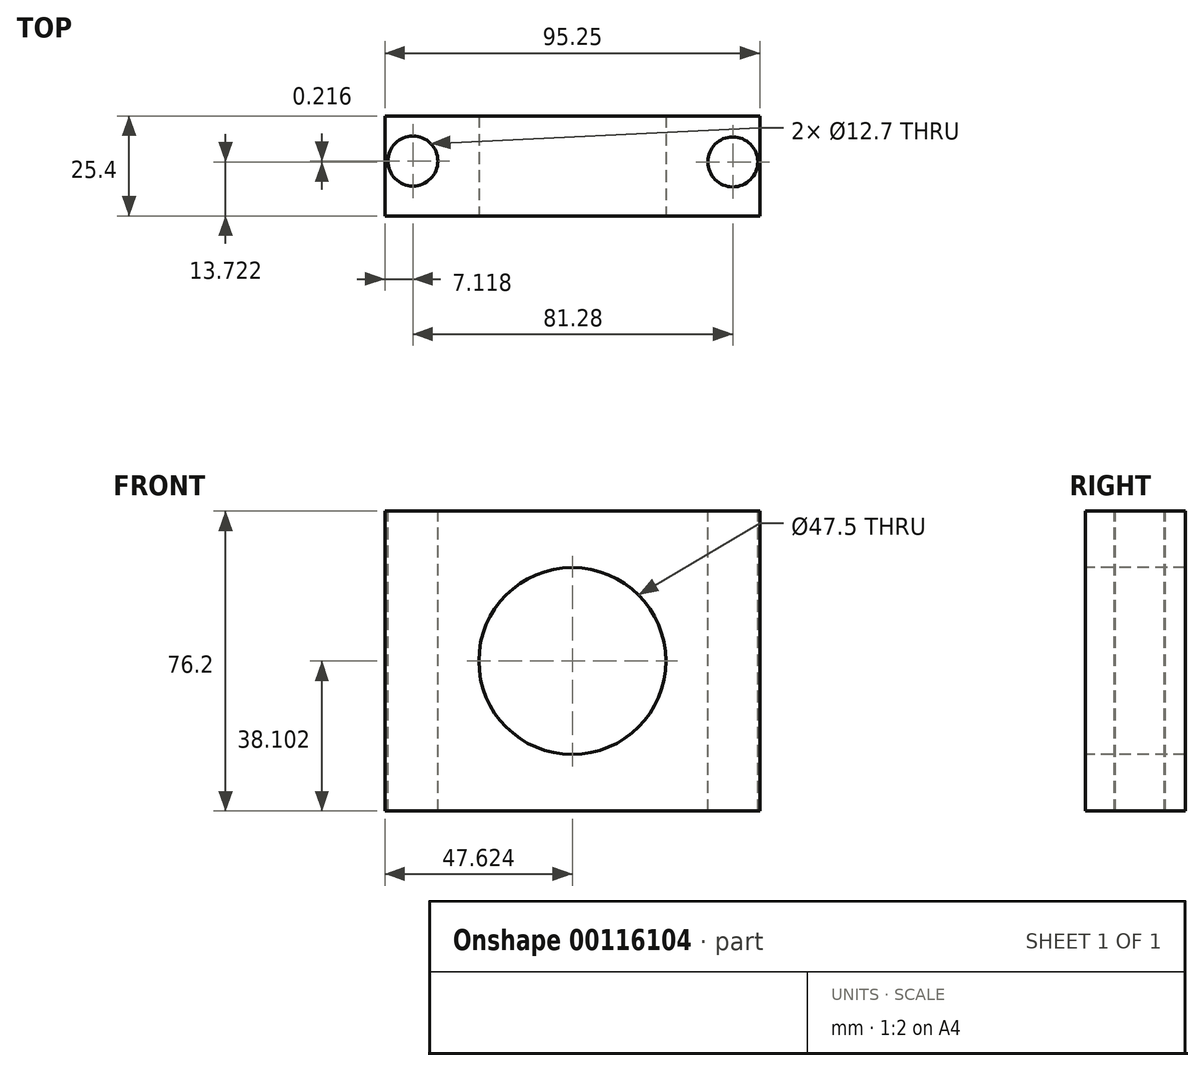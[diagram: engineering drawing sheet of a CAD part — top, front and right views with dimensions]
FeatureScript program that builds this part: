
annotation { "Feature Type Name" : "Feature", "Feature Type Description" : "" }
export const myFeature = defineFeature(function(context is Context, id is Id, definition is map)
    precondition{}
    {
        {
            var Q0;
            Q0=qCreatedBy(makeId("Front.planeOp"),FACE);
            var sketch = newSketch(context, id + "F0", { "sketchPlane" : qUnion([Q0])});
            skLineSegment(sketch, "E0", {"start": v(-44.8, 42.31) * mm, "end": v(-44.8, -33.89) * mm});
            skLineSegment(sketch, "E1", {"start": v(-44.8, -33.89) * mm, "end": v(50.45, -33.89) * mm});
            skLineSegment(sketch, "E2", {"start": v(50.45, -33.89) * mm, "end": v(50.45, 42.31) * mm});
            skLineSegment(sketch, "E3", {"start": v(50.45, 42.31) * mm, "end": v(-44.8, 42.31) * mm});
            skPoint(sketch, "E4", {"position": v(2.82, 42.31) * mm});
            skPoint(sketch, "E5", {"position": v(-44.8, 4.21) * mm});
            skPoint(sketch, "E6", {"position": v(50.45, 4.21) * mm});
            skPoint(sketch, "E7.positionSnap0", {"position": v(2.82, -33.89) * mm});
            skLineSegment(sketch, "E8", {"start": v(2.82, 42.31) * mm, "end": v(2.82, -33.89) * mm, "construction": true});
            skLineSegment(sketch, "E9", {"start": v(-44.8, 4.21) * mm, "end": v(50.45, 4.21) * mm});
            skCircle(sketch, "E10", {"center": v(2.82, 4.21) * mm, "radius": 23.75 * mm});
            skSolve(sketch);
        }
        {
            var Q0;
            Q0 = qSketchRegion(id + "F0", true);
            extrude(context, id + "F1", {"entities" : qUnion([Q0]), "oppositeDirection" : true, "depth" : 25.4 * mm});
        }
        {
            var Q0;
            Q0=makeQuery(id+"F1.opExtrude","SWEPT_FACE",FACE,{"disambiguationData":[OSD([sQuery(id+"F0.wireOp",EDGE,"E3")])]});
            var sketch = newSketch(context, id + "F2", { "sketchPlane" : qUnion([Q0])});
            skCircle(sketch, "E11", {"center": v(43.6, 13.72) * mm, "radius": 6.35 * mm});
            skCircle(sketch, "E12", {"center": v(-37.68, 13.94) * mm, "radius": 6.35 * mm});
            skSolve(sketch);
        }
        {
            var Q0;
            Q0 = qSketchRegion(id + "F2", true);
            extrude(context, id + "F3", {"entities" : qUnion([Q0]), "operationType" : NewBodyOperationType.REMOVE, "oppositeDirection" : true, "depth" : 127 * mm});
        }
    });
